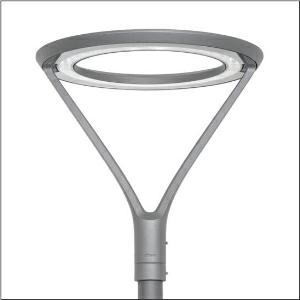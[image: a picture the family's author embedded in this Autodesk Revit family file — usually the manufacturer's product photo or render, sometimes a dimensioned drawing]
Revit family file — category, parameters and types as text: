
# Revit family: dl_r__20___pl1_2s_5xa51283ws008p_a586
name_source: partatom
category: Lighting Fixtures
units: mm (PartAtom-declared; Revit-internal decimal feet)

## family parameters
Cut with Voids When Loaded = No
Host = Face
Light Source = No
Part Type = Normal
Room Calculation Point = No
Round Connector Dimension = Use Diameter
Shared = No

## types (1)
- --- (1 x LED, 4250 lm, 34.3 W, 3000K)
    Apparent Load = 34 VA
    CIE Flux Codes = 33 78 99 100 100
    Color Rendering = 70
    Color Temperature = 3000K
    Default Elevation = 1800 mm
    Description = DL® 20, mast luminaire, primary light control with reflector, highly specular, primary optical cover: cover, of toughened safety glass of clear glass with excellent transmission level, light distribution: PL1.2s, light emission: direct distribution, primary light characteristic: symmetric, installation type: post-top, LED, High Power LED, rated luminous flux: 4.210lm, luminous efficacy: 80lm/W, light colour: 730, colour temperature: 3000K, control gear: ECG Plus, control: overheat protection, power reduction, digital communication interface, constant luminous flux control, time-dependent luminous flux control, flexible luminous flux parameterisation, electronic power reduction, mains connection: 230..240V, 50/60Hz, connection cable pre-assembled, cable length: 5m, start of lifetime: 53W, end of service life: 54W, reduction: 24W, luminaire housing, upper part, of cast aluminium, powder-coated, Siteco® metallic grey (DB 702S), diameter: 690mm, height: 690mm, spigot size: 76mm (post-top), luminaire housing, of cast aluminium, powder-coated, Siteco® metallic grey (DB 702S), equipment: Power, protection rating (complete): IP66, insulation class (complete): insulation class II (safety insulation), certification: CE, ENEC, VDE, impact resistance: IK08, permissible operating ambient temperature: -25..+30°C, standard-compliant lighting for roads and squares, packaging unit: 1 piece

Light Distribution: PL1.2s
    Height = 690 mm
    Lamp = 1 x LED
    Lamp Light Flux = 4250 lm
    Lamp Power = 34.3 W
    Lamp count = 1
    Length = 690 mm
    Luminous efficacy = 124 lm/W
    Manufacturer = Siteco
    ModVariant = No
    Model = 5XA51283WS008P
    Number of Poles = 1
    OnlyDefault = Yes
    Power Factor = 1
    Product Name = DL® 20 | PL1.2s
    Product group = mast luminaire | pylon top
    ProductGroupID = 6100
    Protection Class = Protection class II
    Protection Degree = IP 66
    RLX_Detail_Level = 1
    RLX_Emergency_Light_Flux = 0 lm
    RLX_Emergency_Type = 0
    RLX_Emergency_Type_DB = No
    RlxData = <blob elided: 204533 chars, md5=71238c78>
    Socket = socket
    Standby Power = 0 W
    System Light Flux = 4250 lm
    System Power = 34 W
    Type Comments = factory setting: luminous flux: 100 % | dim-lin: 254 | 464 mA
    Type Image = l_1006001.jpg
    URL = http://relux.com
    VarID = @adj_045917
    Voltage = 0 V
    Weight = 0.00 kg
    Width = 0 mm  [stored 0 ft]

note: [stored X ft] marks values corroborated as IEEE doubles in the binary element streams (Revit-internal decimal feet)

## geometry (parser evidence)
native form markers: Blend x4, Sweep x10
no freeform markers — native parametric forms only
